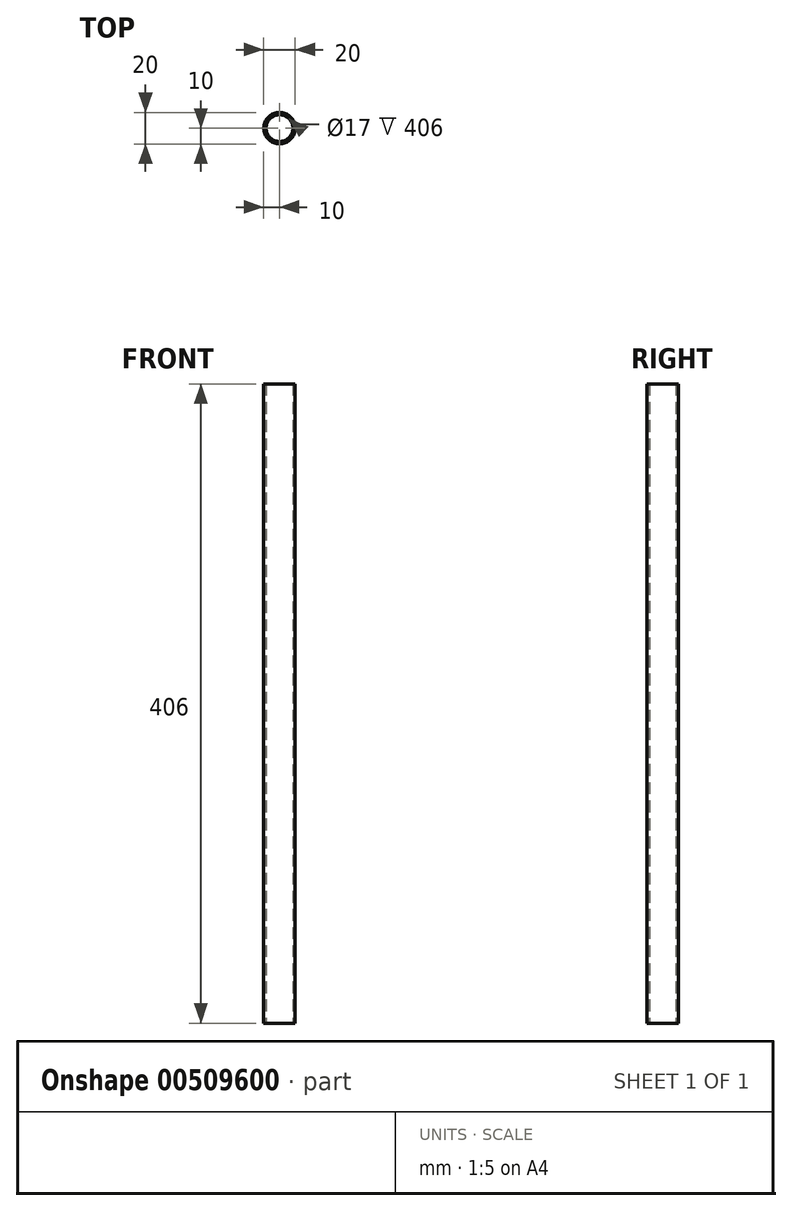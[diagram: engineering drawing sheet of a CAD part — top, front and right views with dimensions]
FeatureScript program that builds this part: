
annotation { "Feature Type Name" : "Feature", "Feature Type Description" : "" }
export const myFeature = defineFeature(function(context is Context, id is Id, definition is map)
    precondition{}
    {
        {
            var Q0;
            Q0=qCreatedBy(makeId("Top.planeOp"),FACE);
            var sketch = newSketch(context, id + "F0", { "sketchPlane" : qUnion([Q0])});
            skCircle(sketch, "E0", {"center": v(0, 0) * mm, "radius": 10 * mm});
            skCircle(sketch, "E1.0", {"center": v(0, 0) * mm, "radius": 8.5 * mm});
            skSolve(sketch);
        }
        {
            var Q0;
            Q0=makeQuery(id+"F0.imprint","IMPRINT",FACE,{"disambiguationData":[TD([[makeQuery(id+"F0.imprint","IMPRINT",EDGE,{"derivedFrom":sQuery(id+"F0.wireOp",EDGE,"E0")}),1.0]])]});
            var Q1;
            Q1=sQuery(id+"F0.wireOp",EDGE,"E1.0");
            var Q2;
            Q2=sQuery(id+"F0.wireOp",EDGE,"E0");
            extrude(context, id + "F1", {"entities" : qUnion([Q0]), "surfaceEntities" : qUnion([Q1, Q2]), "depth" : 406 * mm, "offsetDistance" : 25 * mm});
        }
    });
